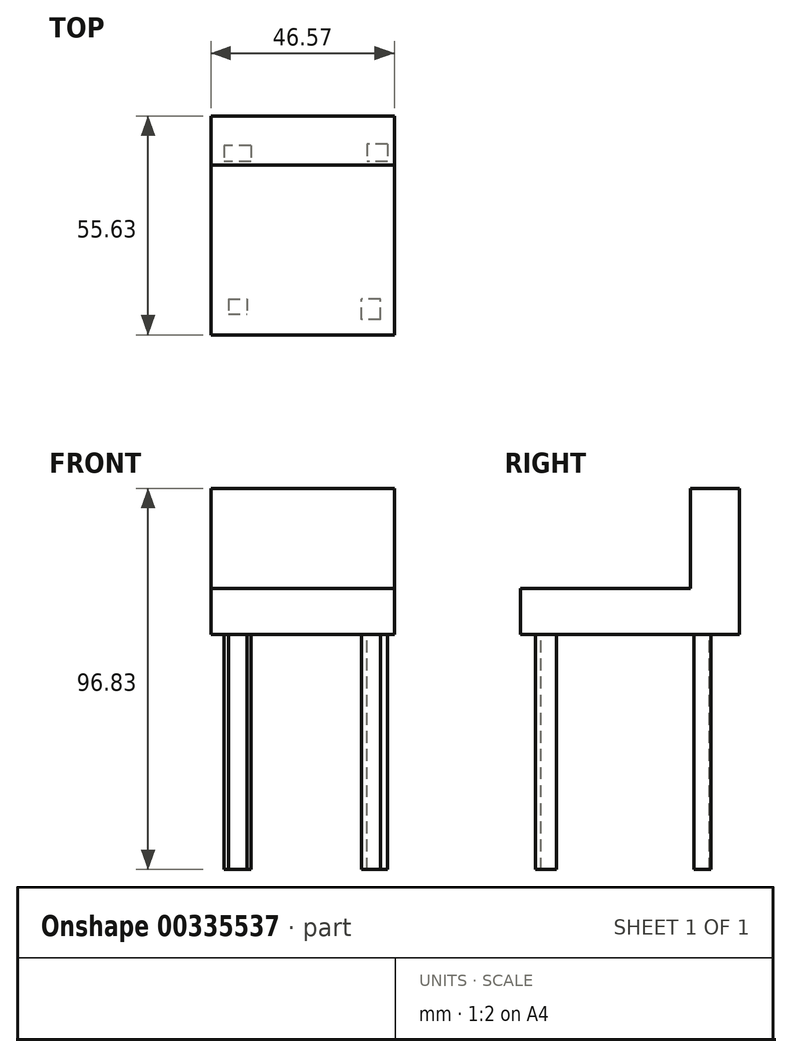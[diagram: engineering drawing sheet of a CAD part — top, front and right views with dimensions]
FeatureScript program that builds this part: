
annotation { "Feature Type Name" : "Feature", "Feature Type Description" : "" }
export const myFeature = defineFeature(function(context is Context, id is Id, definition is map)
    precondition{}
    {
        {
            var Q0;
            Q0=qCreatedBy(makeId("Front.planeOp"),FACE);
            var sketch = newSketch(context, id + "F0", { "sketchPlane" : qUnion([Q0])});
            skLineSegment(sketch, "E0", {"start": v(1.05, 4.55) * mm, "end": v(11.45, 4.55) * mm});
            skLineSegment(sketch, "E1", {"start": v(11.45, 4.55) * mm, "end": v(12.2, 7.4) * mm});
            skLineSegment(sketch, "E2", {"start": v(12.2, 7.4) * mm, "end": v(1.27, 7.4) * mm});
            skLineSegment(sketch, "E3", {"start": v(1.05, 4.55) * mm, "end": v(1.27, 7.4) * mm});
            skLineSegment(sketch, "E4", {"start": v(11.45, 4.55) * mm, "end": v(16.03, 2.34) * mm});
            skLineSegment(sketch, "E5", {"start": v(12.2, 7.4) * mm, "end": v(17.6, 4.83) * mm});
            skLineSegment(sketch, "E6", {"start": v(17.6, 4.83) * mm, "end": v(16.03, 2.34) * mm});
            skLineSegment(sketch, "E7", {"start": v(1.27, 7.4) * mm, "end": v(-2.18, 6.2) * mm});
            skLineSegment(sketch, "E8", {"start": v(-2.18, 6.2) * mm, "end": v(-2.18, 3.65) * mm});
            skLineSegment(sketch, "E9", {"start": v(-2.18, 3.65) * mm, "end": v(1.05, 4.55) * mm});
            skLineSegment(sketch, "E10", {"start": v(16.03, 2.34) * mm, "end": v(-0.56, 2.34) * mm});
            skLineSegment(sketch, "E11", {"start": v(-0.56, 2.34) * mm, "end": v(-2.18, 3.65) * mm});
            skSolve(sketch);
        }
        {
            var Q0;
            Q0 = qSketchRegion(id + "F0", true);
            extrude(context, id + "F1", {"entities" : qUnion([Q0]), "depth" : 4.11 * mm});
        }
        {
            var Q0;
            Q0=makeQuery(id+"F1.opExtrude","SWEPT_BODY",BODY,{"disambiguationData":[OSD([sQuery(id+"F0.wireOp",EDGE,"E2"),sQuery(id+"F0.wireOp",EDGE,"E5"),sQuery(id+"F0.wireOp",EDGE,"E6"),sQuery(id+"F0.wireOp",EDGE,"E7"),sQuery(id+"F0.wireOp",EDGE,"E8"),sQuery(id+"F0.wireOp",EDGE,"E10"),sQuery(id+"F0.wireOp",EDGE,"E11")])]});
            deleteBodies(context, id + "F2", {"entities" : qUnion([Q0])});
        }
        {
            var Q0;
            Q0=qCreatedBy(makeId("Front.planeOp"),FACE);
            var sketch = newSketch(context, id + "F3", { "sketchPlane" : qUnion([Q0])});
            skLineSegment(sketch, "E12.bottom", {"start": v(5.12, 96.24) * mm, "end": v(-16.05, 96.24) * mm});
            skLineSegment(sketch, "E12.top", {"start": v(5.12, 107.98) * mm, "end": v(-16.05, 107.98) * mm});
            skLineSegment(sketch, "E12.left", {"start": v(5.12, 96.24) * mm, "end": v(5.12, 107.98) * mm});
            skLineSegment(sketch, "E12.right", {"start": v(-16.05, 96.24) * mm, "end": v(-16.05, 107.98) * mm});
            skSolve(sketch);
        }
        {
            var Q0;
            Q0=makeQuery(id+"F3.imprint","IMPRINT",FACE,{"disambiguationData":[TD([[makeQuery(id+"F3.imprint","IMPRINT",EDGE,{"derivedFrom":sQuery(id+"F3.wireOp",EDGE,"E12.bottom")}),-1.0]])]});
            var sketch = newSketch(context, id + "F4", { "sketchPlane" : qUnion([Q0])});
            skLineSegment(sketch, "E13.bottom", {"start": v(5.06, 107.96) * mm, "end": v(3.26, 107.96) * mm});
            skLineSegment(sketch, "E13.top", {"start": v(5.06, 96.39) * mm, "end": v(3.26, 96.39) * mm});
            skLineSegment(sketch, "E13.left", {"start": v(5.06, 107.96) * mm, "end": v(5.06, 96.39) * mm});
            skLineSegment(sketch, "E13.right", {"start": v(3.26, 107.96) * mm, "end": v(3.26, 96.39) * mm});
            skSolve(sketch);
        }
        {
            var Q0;
            Q0 = qSketchRegion(id + "F4", true);
            extrude(context, id + "F5", {"entities" : qUnion([Q0]), "depth" : 25.4 * mm});
        }
        {
            var Q0;
            Q0=makeQuery(id+"F3.imprint","IMPRINT",FACE,{"disambiguationData":[TD([[makeQuery(id+"F3.imprint","IMPRINT",EDGE,{"derivedFrom":sQuery(id+"F3.wireOp",EDGE,"E12.bottom")}),-1.0]])]});
            extrude(context, id + "F6", {"entities" : qUnion([Q0]), "operationType" : NewBodyOperationType.ADD, "depth" : 25.4 * mm});
        }
        {
            var Q0;
            Q0=makeQuery(id+"F6.opExtrude","SWEPT_FACE",FACE,{"disambiguationData":[OSD([sQuery(id+"F3.wireOp",EDGE,"E12.top")])]});
            var sketch = newSketch(context, id + "F7", { "sketchPlane" : qUnion([Q0])});
            skLineSegment(sketch, "E14.bottom", {"start": v(5.12, 0) * mm, "end": v(-16.05, 0) * mm});
            skLineSegment(sketch, "E14.top", {"start": v(5.12, -7.6) * mm, "end": v(-16.05, -7.6) * mm});
            skLineSegment(sketch, "E14.left", {"start": v(5.12, 0) * mm, "end": v(5.12, -7.6) * mm});
            skLineSegment(sketch, "E14.right", {"start": v(-16.05, 0) * mm, "end": v(-16.05, -7.6) * mm});
            skSolve(sketch);
        }
        {
            var Q0;
            Q0 = qSketchRegion(id + "F7", true);
            extrude(context, id + "F8", {"entities" : qUnion([Q0]), "operationType" : NewBodyOperationType.ADD, "depth" : 25.4 * mm});
        }
        {
            var Q0;
            Q0=makeQuery(id+"F6.boolean.opBoolean","MERGE",FACE,{"derivedFrom":[makeQuery(id+"F5.opExtrude","CAP_FACE",FACE,{"disambiguationData":[OSD([sQuery(id+"F4.wireOp",EDGE,"E13.bottom"),sQuery(id+"F4.wireOp",EDGE,"E13.top"),sQuery(id+"F4.wireOp",EDGE,"E13.left"),sQuery(id+"F4.wireOp",EDGE,"E13.right")])],"isStart":false}),makeQuery(id+"F6.opExtrude","CAP_FACE",FACE,{"disambiguationData":[OSD([sQuery(id+"F3.wireOp",EDGE,"E12.bottom"),sQuery(id+"F3.wireOp",EDGE,"E12.top"),sQuery(id+"F3.wireOp",EDGE,"E12.left"),sQuery(id+"F3.wireOp",EDGE,"E12.right")])],"isStart":false})]});
            extrude(context, id + "F9", {"entities" : qUnion([Q0]), "operationType" : NewBodyOperationType.ADD, "depth" : 25.4 * mm});
        }
        {
            var Q0;
            {var subQ0=sQuery(id+"F3.wireOp",EDGE,"E12.right");Q0=makeQuery(id+"F9.boolean.opBoolean","MERGE",FACE,{"derivedFrom":[makeQuery(id+"F8.boolean.opBoolean","MERGE",FACE,{"derivedFrom":[makeQuery(id+"F6.opExtrude","SWEPT_FACE",FACE,{"disambiguationData":[OSD([subQ0])]}),makeQuery(id+"F8.opExtrude","SWEPT_FACE",FACE,{"disambiguationData":[OSD([sQuery(id+"F7.wireOp",EDGE,"E14.right")])]})]}),makeQuery(id+"F9.opExtrude","SWEPT_FACE",FACE,{"disambiguationData":[OSD([subQ0])]})]});}
            extrude(context, id + "F10", {"entities" : qUnion([Q0]), "operationType" : NewBodyOperationType.ADD, "depth" : 25.4 * mm});
        }
        {
            var Q0;
            {var subQ0=sQuery(id+"F3.wireOp",EDGE,"E12.bottom");Q0=makeQuery(id+"F10.boolean.opBoolean","MERGE",FACE,{"derivedFrom":[makeQuery(id+"F9.boolean.opBoolean","MERGE",FACE,{"derivedFrom":[makeQuery(id+"F6.opExtrude","SWEPT_FACE",FACE,{"disambiguationData":[OSD([subQ0])]}),makeQuery(id+"F9.opExtrude","SWEPT_FACE",FACE,{"disambiguationData":[OSD([subQ0])]})]}),makeQuery(id+"F10.opExtrude","SWEPT_FACE",FACE,{"disambiguationData":[OSD([subQ0,sQuery(id+"F3.wireOp",EDGE,"E12.right")])]})]});}
            var sketch = newSketch(context, id + "F11", { "sketchPlane" : qUnion([Q0])});
            skLineSegment(sketch, "E15.bottom", {"start": v(3.4, 2.3) * mm, "end": v(-1.76, 2.3) * mm});
            skLineSegment(sketch, "E15.top", {"start": v(3.4, 6.7) * mm, "end": v(-1.76, 6.7) * mm});
            skLineSegment(sketch, "E15.left", {"start": v(3.4, 2.3) * mm, "end": v(3.4, 6.7) * mm});
            skLineSegment(sketch, "E15.right", {"start": v(-1.76, 2.3) * mm, "end": v(-1.76, 6.7) * mm});
            skLineSegment(sketch, "E16.bottom", {"start": v(-31.33, 2.73) * mm, "end": v(-38.1, 2.73) * mm});
            skLineSegment(sketch, "E16.top", {"start": v(-31.33, 6.7) * mm, "end": v(-38.1, 6.7) * mm});
            skLineSegment(sketch, "E16.left", {"start": v(-31.33, 2.73) * mm, "end": v(-31.33, 6.7) * mm});
            skLineSegment(sketch, "E16.right", {"start": v(-38.1, 2.73) * mm, "end": v(-38.1, 6.7) * mm});
            skLineSegment(sketch, "E17.bottom", {"start": v(1.6, 46.88) * mm, "end": v(-3.26, 46.88) * mm});
            skLineSegment(sketch, "E17.top", {"start": v(1.6, 41.63) * mm, "end": v(-3.26, 41.63) * mm});
            skLineSegment(sketch, "E17.left", {"start": v(1.6, 46.88) * mm, "end": v(1.6, 41.63) * mm});
            skLineSegment(sketch, "E17.right", {"start": v(-3.26, 46.88) * mm, "end": v(-3.26, 41.63) * mm});
            skLineSegment(sketch, "E18.bottom", {"start": v(-37.05, 41.63) * mm, "end": v(-32.35, 41.63) * mm});
            skLineSegment(sketch, "E18.top", {"start": v(-37.05, 45.52) * mm, "end": v(-32.35, 45.52) * mm});
            skLineSegment(sketch, "E18.left", {"start": v(-37.05, 41.63) * mm, "end": v(-37.05, 45.52) * mm});
            skLineSegment(sketch, "E18.right", {"start": v(-32.35, 41.63) * mm, "end": v(-32.35, 45.52) * mm});
            skSolve(sketch);
        }
        {
            var Q0;
            Q0 = qSketchRegion(id + "F11", true);
            extrude(context, id + "F12", {"entities" : qUnion([Q0]), "operationType" : NewBodyOperationType.ADD, "depth" : 59.69 * mm});
        }
        {
            var Q0;
            {var subQ0=sQuery(id+"F7.wireOp",EDGE,"E14.bottom");var subQ1=sQuery(id+"F3.wireOp",EDGE,"E12.right");Q0=makeQuery(id+"F10.boolean.opBoolean","MERGE",FACE,{"derivedFrom":[makeQuery(id+"F8.boolean.opBoolean","MERGE",FACE,{"derivedFrom":[makeQuery(id+"F6.boolean.opBoolean","MERGE",FACE,{"derivedFrom":[makeQuery(id+"F5.opExtrude","CAP_FACE",FACE,{"disambiguationData":[OSD([sQuery(id+"F4.wireOp",EDGE,"E13.bottom"),sQuery(id+"F4.wireOp",EDGE,"E13.top"),sQuery(id+"F4.wireOp",EDGE,"E13.left"),sQuery(id+"F4.wireOp",EDGE,"E13.right")])],"isStart":true}),makeQuery(id+"F6.opExtrude","CAP_FACE",FACE,{"disambiguationData":[OSD([sQuery(id+"F3.wireOp",EDGE,"E12.bottom"),sQuery(id+"F3.wireOp",EDGE,"E12.top"),sQuery(id+"F3.wireOp",EDGE,"E12.left"),subQ1])],"isStart":true})]}),makeQuery(id+"F8.opExtrude","SWEPT_FACE",FACE,{"disambiguationData":[OSD([subQ0])]})]}),makeQuery(id+"F10.opExtrude","SWEPT_FACE",FACE,{"disambiguationData":[OSD([subQ1,subQ0,sQuery(id+"F7.wireOp",EDGE,"E14.right")])]})]});}
            extrude(context, id + "F13", {"entities" : qUnion([Q0]), "operationType" : NewBodyOperationType.ADD, "depth" : 4.83 * mm});
        }
    });
